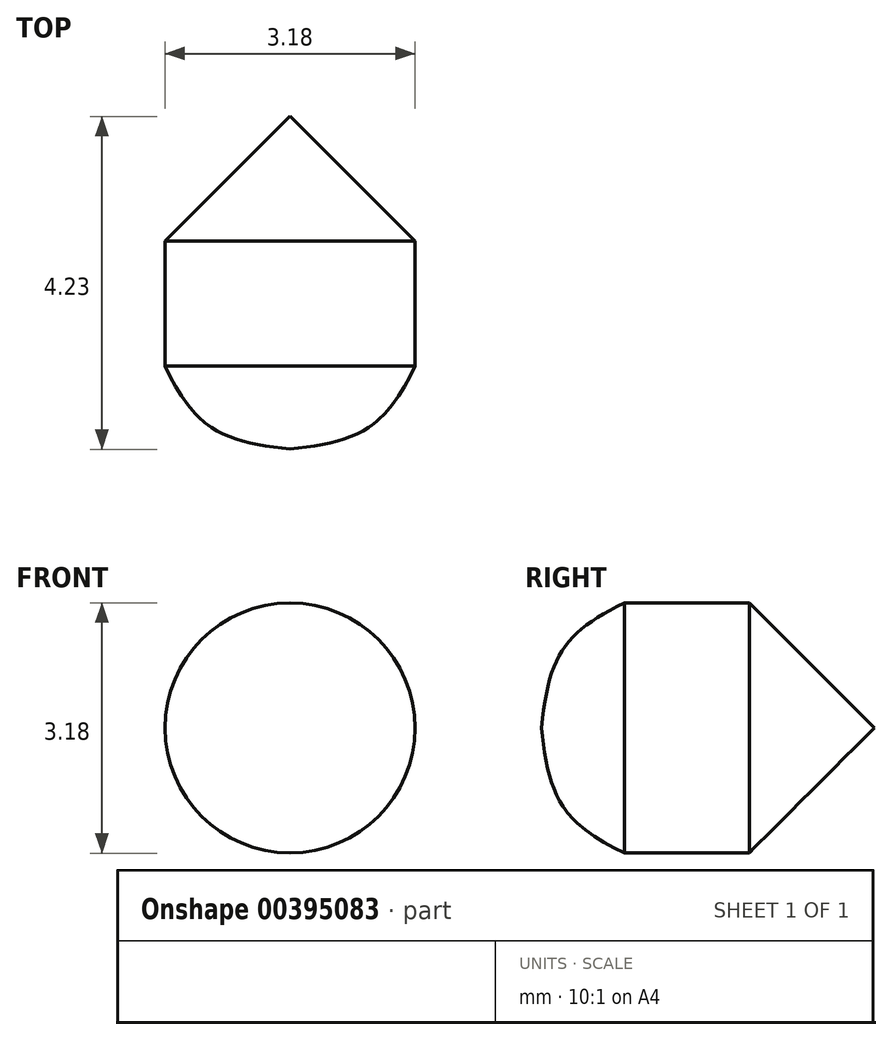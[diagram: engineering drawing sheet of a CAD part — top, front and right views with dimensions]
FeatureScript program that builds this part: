
annotation { "Feature Type Name" : "Feature", "Feature Type Description" : "" }
export const myFeature = defineFeature(function(context is Context, id is Id, definition is map)
    precondition{}
    {
        {
            var Q0;
            Q0=qCreatedBy(makeId("Right.planeOp"),FACE);
            var sketch = newSketch(context, id + "F0", { "sketchPlane" : qUnion([Q0])});
            skLineSegment(sketch, "E0.bottom", {"start": v(0.8, 1.59) * mm, "end": v(-0.8, 1.59) * mm});
            skLineSegment(sketch, "E0.top", {"start": v(0.8, -1.59) * mm, "end": v(-0.8, -1.59) * mm});
            skLineSegment(sketch, "E0.left", {"start": v(0.8, 1.59) * mm, "end": v(0.8, -1.59) * mm});
            skLineSegment(sketch, "E0.right", {"start": v(-0.8, 1.59) * mm, "end": v(-0.8, -1.59) * mm});
            skPoint(sketch, "E0.middle", {"position": v(0, 0) * mm});
            skLineSegment(sketch, "E1", {"start": v(2.38, 0) * mm, "end": v(0.8, 1.59) * mm});
            skLineSegment(sketch, "E2", {"start": v(2.38, 0) * mm, "end": v(0.8, -1.59) * mm});
            skFitSpline(sketch, "E3", {"points": [v(-0.8, 1.59) * mm, v(-1.85, 0) * mm], "startDerivative": vector(-2.21, -1.08) * mm, "endDerivative": vector(-0.27, -2.82) * mm});
            skLineSegment(sketch, "E4", {"start": v(-1.85, 0) * mm, "end": v(-0.8, 0) * mm});
            skFitSpline(sketch, "E5.MirrorCS", {"points": [v(-0.8, -1.59) * mm, v(-1.85, 0) * mm], "startDerivative": vector(-2.21, 1.08) * mm, "endDerivative": vector(-0.27, 2.82) * mm});
            skLineSegment(sketch, "E6", {"start": v(-0.8, 0) * mm, "end": v(0.8, 0) * mm});
            skLineSegment(sketch, "E7", {"start": v(0.8, 0) * mm, "end": v(2.38, 0) * mm});
            skSolve(sketch);
        }
        {
            var Q0;
            {var subQ0=sQuery(id+"F0.wireOp",EDGE,"E3");Q0=makeQuery(id+"F0.imprint","IMPRINT",FACE,{"disambiguationData":[TD([[makeQuery(id+"F0.imprint","IMPRINT",EDGE,{"derivedFrom":subQ0}),1.0]])]});}
            var Q1;
            {var subQ0=sQuery(id+"F0.wireOp",EDGE,"E0.bottom");Q1=makeQuery(id+"F0.imprint","IMPRINT",FACE,{"disambiguationData":[TD([[makeQuery(id+"F0.imprint","IMPRINT",EDGE,{"derivedFrom":subQ0}),1.0]])]});}
            var Q2;
            {var subQ0=sQuery(id+"F0.wireOp",EDGE,"E1");Q2=makeQuery(id+"F0.imprint","IMPRINT",FACE,{"disambiguationData":[TD([[makeQuery(id+"F0.imprint","IMPRINT",EDGE,{"derivedFrom":subQ0}),1.0]])]});}
            var Q3;
            Q3=sQuery(id+"F0.wireOp",EDGE,"E6");
            revolve(context, id + "F1", {"entities" : qUnion([Q0, Q1, Q2]), "axis" : qUnion([Q3]), "revolveType" : RevolveType.FULL});
        }
    });
